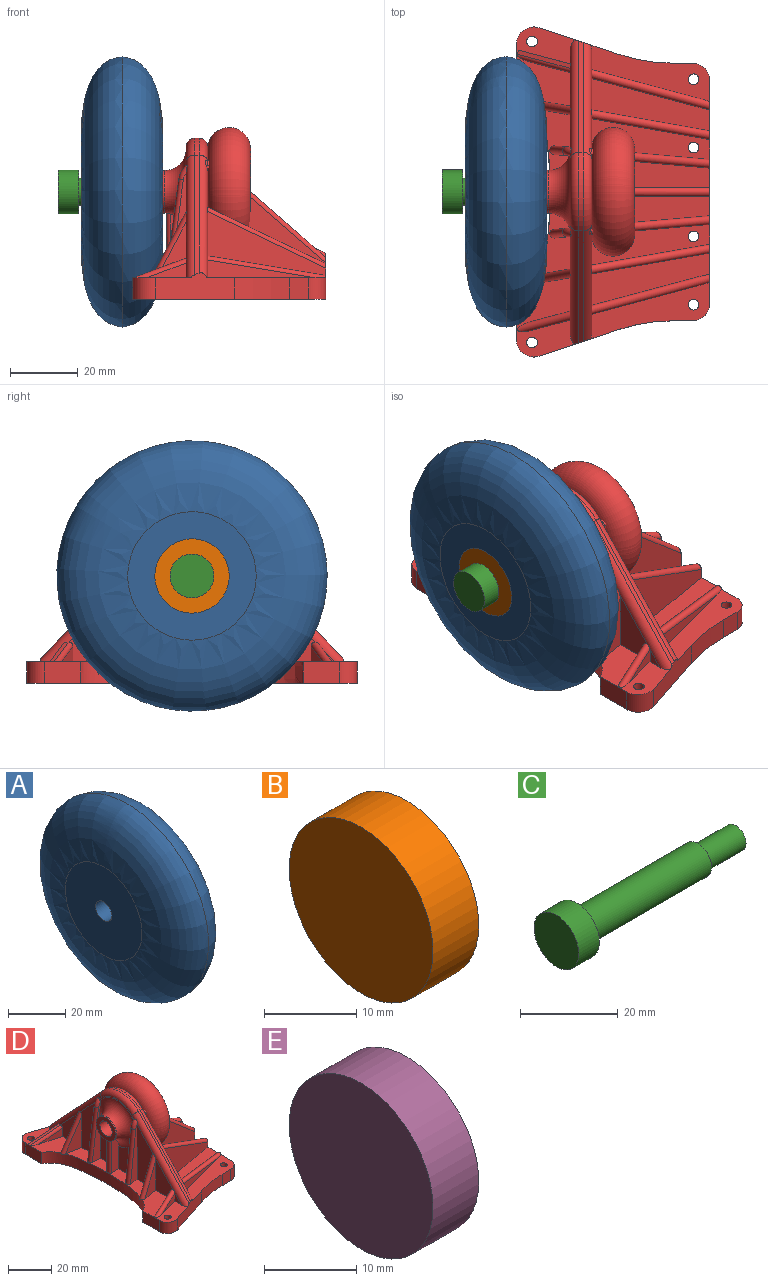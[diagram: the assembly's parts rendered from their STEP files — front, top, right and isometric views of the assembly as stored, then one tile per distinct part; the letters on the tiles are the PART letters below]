
ASSEMBLY  parts=5 mates=4
PART A: 5 faces, bbox 24x80x80 mm
  f0: cylinder r=4mm len=24mm, axis (-1,0,0), area 603.2mm2, adj f1,f4
  f1: plane 38x38mm, normal (1,0,0), area 1083.8mm2, adj f0,f2
  f2: revolved ~80x80mm, area 5252.7mm2, adj f1,f3
  f3: revolved ~80x80mm, area 5252.7mm2, adj f2,f4
  f4: plane 38x38mm, normal (-1,0,0), area 1083.8mm2, adj f0,f3
PART B: 3 faces, bbox 7x22x22 mm
  f0: plane 22x22mm, normal (1,0,0), area 380.1mm2, adj f1
  f1: cylinder r=11mm len=22mm, axis (-1,0,0), area 483.8mm2, adj f0,f2
  f2: plane 22x22mm, normal (-1,0,0), area 380.1mm2, adj f1
PART C: 7 faces, bbox 52x13x13 mm
  f0: cylinder r=6.5mm len=13mm, axis (1,0,0), area 245mm2, adj f1,f6
  f1: plane 13x13mm, normal (-1,0,0), area 132.7mm2, adj f0
  f2: plane 6x6mm, normal (1,0,0), area 28.3mm2, adj f3
  f3: cylinder r=3mm len=11mm, axis (1,0,0), area 207.3mm2, adj f2,f4
  f4: plane 8x8mm, normal (1,0,0), area 22mm2, adj f3,f5
  f5: cylinder r=4mm len=35mm, axis (1,0,0), area 879.6mm2, adj f4,f6
  f6: plane 13x13mm, normal (1,0,0), area 82.5mm2, adj f0,f5
PART D: 125 faces, bbox 58.6x98.1x52.8 mm
  f0: cylinder r=1.27mm len=29.7mm, axis (0.91,0,-0.42), area 124mm2, adj f1,f2,f50,f67,f68,f74
  f1: plane 35.02x19.43mm, normal (0,1,0), area 470mm2, adj f0,f27,f30,f32,f50,f74
  f2: plane 35.02x19.43mm, normal (0,-1,0), area 470mm2, adj f0,f30,f40,f45,f50,f74
  f3: plane 34.93x33.36mm, normal (-0.09,1,0), area 677.7mm2, adj f26,f30,f40,f45,f50,f109,f110
  f4: plane 35.43x33.46mm, normal (0.09,-1,0), area 688.9mm2, adj f39,f48,f50,f61,f63,f109,f110,f111
  f5: plane 34.97x19.63mm, normal (0.17,-0.98,0), area 399.1mm2, adj f34,f37,f50,f63,f123
  f6: plane 34.93x19.39mm, normal (-0.17,0.98,0), area 391.6mm2, adj f39,f48,f50,f123
  f7: plane 31.75x8.51mm, normal (0.26,-0.97,0), area 86.5mm2, adj f33,f34,f120
  f8: plane 31.09x8.33mm, normal (-0.26,0.97,0), area 83mm2, adj f34,f37,f120
  f9: plane 34.93x33.36mm, normal (-0.09,-1,0), area 677.7mm2, adj f26,f27,f30,f32,f50,f106,f107
  f10: plane 35.43x33.46mm, normal (0.09,1,0), area 688.9mm2, adj f16,f24,f25,f43,f50,f106,f107,f108
  f11: plane 34.97x19.63mm, normal (0.17,0.98,0), area 399.1mm2, adj f16,f20,f21,f50,f119
  f12: plane 34.93x19.39mm, normal (-0.17,-0.98,0), area 391.6mm2, adj f24,f25,f50,f119
  f13: plane 31.75x8.51mm, normal (0.26,0.97,0), area 86.5mm2, adj f20,f55,f116
  f14: plane 31.09x8.33mm, normal (-0.26,-0.97,0), area 83mm2, adj f20,f21,f116
  f15: plane 97.66x57.16mm, normal (0,0,-1), area 4244.1mm2, adj f46,f47,f50,f51,f52,f53,f54,f76
  f16: cylinder r=2.54mm len=36.96mm, axis (0,-0.68,0.73), area 184.4mm2, adj f10,f11,f20,f24,f26,f52,f55,f58
  f17: cylinder r=2.54mm len=37.76mm, axis (0,0.68,-0.73), area 189.7mm2, adj f18,f19,f22,f29,f41,f52,f58,f64
  f18: plane 18.03x11.41mm, normal (-1,0,0), area 125.3mm2, adj f17,f19,f88,f92,f117,f118
  f19: plane 23.53x17.25mm, normal (0,0,1), area 265mm2, adj f17,f18,f29,f52,f53,f76,f88,f91
  f20: plane 19.48x18.26mm, normal (1,0,0), area 152.7mm2, adj f11,f13,f14,f16,f21,f55,f116
  f21: plane 35.06x15.61mm, normal (0,0,1), area 269.9mm2, adj f11,f14,f20,f50,f116
  f22: plane 30.79x10.42mm, normal (-1,0,0), area 246.5mm2, adj f17,f23,f86,f89,f118
  f23: plane 49.04x9.21mm, normal (0,0,1), area 270.8mm2, adj f22,f28,f42,f49,f76,f77,f78,f79
  f24: plane 31.45x9.97mm, normal (1,0,0), area 239.9mm2, adj f10,f12,f16,f25,f43,f119
  f25: plane 34.93x12.06mm, normal (0,0,1), area 252.2mm2, adj f10,f12,f24,f50,f101
  f26: plane 20.52x5.66mm, normal (1,0,0), area 14.8mm2, adj f3,f9,f16,f30,f62,f63,f107,f110
  f27: plane 17.72x8.84mm, normal (1,0,0), area 127.6mm2, adj f1,f9,f30,f32
  f28: plane 18.51x9.4mm, normal (-1,0,0), area 137.7mm2, adj f23,f31,f78,f87
  f29: plane 4.42x4.13mm, normal (-1,0,0), area 9.1mm2, adj f17,f19,f91
  f30: torus R=12.7mm, axis (-1,0,0), area 409.3mm2, adj f1,f2,f3,f9,f26,f27,f40,f74
  f31: torus R=12.7mm, axis (1,0,0), area 480.9mm2, adj f28,f41,f42,f60,f77,f78,f80,f87
  f32: plane 34.93x8.84mm, normal (0,0,1), area 255.5mm2, adj f1,f9,f27,f50
  f33: plane 35.23x16.83mm, normal (0,0,1), area 262.3mm2, adj f7,f34,f47,f50,f54,f63,f99,f103
  f34: plane 19.48x18.26mm, normal (1,0,0), area 152.7mm2, adj f5,f7,f8,f33,f37,f63,f120
  f35: plane 4.42x4.13mm, normal (-1,0,0), area 9.1mm2, adj f36,f44,f85,f121
  f36: plane 23.53x17.25mm, normal (0,0,1), area 266.1mm2, adj f35,f38,f44,f46,f47,f76,f83,f84
  f37: plane 35.06x15.61mm, normal (0,0,1), area 269.9mm2, adj f5,f8,f34,f50,f120
  f38: plane 18.03x11.41mm, normal (-1,0,0), area 125.3mm2, adj f36,f44,f83,f84,f121,f122
  f39: plane 34.93x12.06mm, normal (0,0,1), area 252.2mm2, adj f4,f6,f48,f50,f97
  f40: plane 17.72x8.84mm, normal (1,0,0), area 127.6mm2, adj f2,f3,f30,f45
  f41: plane 22.51x6.67mm, normal (-1,0,0), area 16.7mm2, adj f17,f31,f44,f64,f113,f114
  f42: plane 18.51x9.4mm, normal (-1,0,0), area 137.7mm2, adj f23,f31,f77,f80
  f43: torus R=12.7mm, axis (-1,0,0), area 3183.7mm2, adj f10,f24
  f44: cylinder r=2.54mm len=37.76mm, axis (0,0.68,0.73), area 190.1mm2, adj f35,f36,f38,f41,f47,f49,f56,f64
  f45: plane 34.93x8.84mm, normal (0,0,1), area 255.5mm2, adj f2,f3,f40,f50
  f46: plane 10.9x6.35mm, normal (-1,0,0), area 69.2mm2, adj f15,f36,f76,f95
  f47: plane 23.59x7.86mm, normal (0.32,-0.95,0), area 162.9mm2, adj f15,f33,f36,f44,f56,f63,f95,f105
  f48: plane 31.45x9.97mm, normal (1,0,0), area 239.9mm2, adj f4,f6,f39,f61,f63,f123
  f49: plane 30.79x10.42mm, normal (-1,0,0), area 246.5mm2, adj f23,f44,f79,f82,f122
  f50: plane 66.3x13.92mm, normal (1,0,0), area 488.6mm2, adj f0,f1,f2,f3,f4,f5,f6,f9
  f51: plane 6.35x5.73mm, normal (0,1,0), area 36.4mm2, adj f15,f55,f102,f104
  f52: plane 23.59x7.86mm, normal (0.32,0.95,0), area 162.9mm2, adj f15,f16,f17,f19,f55,f58,f94,f104
  f53: plane 10.9x6.35mm, normal (-1,0,0), area 69.2mm2, adj f15,f19,f76,f94
  f54: plane 6.35x5.73mm, normal (0,-1,0), area 36.4mm2, adj f15,f33,f103,f105
  f55: plane 35.23x16.83mm, normal (0,0,1), area 262.3mm2, adj f13,f16,f20,f50,f51,f52,f96,f102
  f56: plane 35.34x33.07mm, normal (0,-0.73,0.68), area 61.1mm2, adj f44,f47,f57,f63
  f57: cylinder r=15.88mm len=23.18mm, axis (1,0,0), area 33mm2, adj f56,f58,f62,f64
  f58: plane 35.34x33.07mm, normal (0,0.73,0.68), area 61.1mm2, adj f16,f17,f52,f57
  f59: plane 12.7x12.7mm, normal (-1,0,0), area 76.4mm2, adj f60,f65
  f60: cylinder r=6.35mm len=12.7mm, axis (-1,0,0), area 25.3mm2, adj f31,f59
  f61: torus R=12.7mm, axis (-1,0,0), area 3183.7mm2, adj f4,f48
  f62: torus R=13.33mm, axis (-1,0,0), area 97.7mm2, adj f16,f26,f57,f63
  f63: cylinder r=2.54mm len=36.96mm, axis (0,-0.68,-0.73), area 184.4mm2, adj f4,f5,f26,f33,f34,f47,f48,f56
  f64: torus R=13.33mm, axis (1,0,0), area 97.7mm2, adj f17,f41,f44,f57
  f65: cylinder r=4mm len=10.16mm, axis (1,0,0), area 255.3mm2, adj f59,f66
  f66: plane 8x8mm, normal (-1,0,0), area 22mm2, adj f65,f75
  f67: plane 7.4x5.22mm, normal (0,0.5,0.87), area 33.6mm2, adj f0,f68,f72,f73,f74
  f68: plane 7.4x5.22mm, normal (0,-0.5,0.87), area 33.6mm2, adj f0,f67,f69,f73,f74
  f69: plane 5.8x5.77mm, normal (0,-1,0), area 32.6mm2, adj f68,f70,f73,f74
  f70: plane 5.8x5mm, normal (0,-0.5,-0.87), area 32.6mm2, adj f69,f71,f73,f74
  f71: plane 5.8x5mm, normal (0,0.5,-0.87), area 32.6mm2, adj f70,f72,f73,f74
  f72: plane 5.8x5.77mm, normal (0,1,0), area 32.6mm2, adj f67,f71,f73,f74
  f73: plane 11.55x10mm, normal (1,0,0), area 58.3mm2, adj f67,f68,f69,f70,f71,f72,f75
  f74: torus R=4.02mm, axis (-1,0,0), area 76.4mm2, adj f0,f1,f2,f30,f67,f68,f69,f70
  f75: cylinder r=3mm len=6mm, axis (-1,0,0), area 78.4mm2, adj f66,f73
  f76: extruded ~65.71x9.96mm, area 456.5mm2, adj f15,f19,f23,f36,f46,f53,f81,f90
  f77: plane 19.02x4.67mm, normal (0,-1,0), area 78.9mm2, adj f23,f31,f42,f124
  f78: plane 19.02x4.67mm, normal (0,1,0), area 78.9mm2, adj f23,f28,f31,f124
  f79: plane 31.23x4.64mm, normal (0.09,-1,0), area 80.9mm2, adj f23,f44,f49,f114,f115
  f80: plane 31.49x4.85mm, normal (-0.09,1,0), area 85.5mm2, adj f23,f31,f42,f114,f115
  f81: plane 2.27x1.45mm, normal (0,0,-1), area 1.6mm2, adj f76,f82,f122
  f82: plane 17.38x9.11mm, normal (-0.17,0.98,0), area 80.4mm2, adj f23,f49,f81,f122
  f83: plane 16.54x8.67mm, normal (0.17,-0.98,0), area 72.8mm2, adj f36,f38,f122
  f84: plane 12.33x4.61mm, normal (-0.26,0.97,0), area 29.4mm2, adj f36,f38,f121
  f85: plane 11.67x4.36mm, normal (0.26,-0.97,0), area 26.4mm2, adj f35,f36,f121
  f86: plane 31.23x4.64mm, normal (0.09,1,0), area 80.9mm2, adj f17,f22,f23,f112,f113
  f87: plane 31.49x4.85mm, normal (-0.09,-1,0), area 85.5mm2, adj f23,f28,f31,f112,f113
  f88: plane 16.54x8.67mm, normal (0.17,0.98,0), area 72.8mm2, adj f18,f19,f118
  f89: plane 17.38x9.11mm, normal (-0.17,-0.98,0), area 80.4mm2, adj f22,f23,f90,f118
  f90: plane 2.27x1.45mm, normal (0,0,-1), area 1.6mm2, adj f76,f89,f118
  f91: plane 15.45x5.77mm, normal (0.26,0.97,0), area 45.3mm2, adj f17,f19,f29,f93
  f92: plane 12.33x4.61mm, normal (-0.26,-0.97,0), area 29.4mm2, adj f18,f19,f117
  f93: plane 15.78x5.83mm, normal (-0.33,0.09,0.94), area 21.7mm2, adj f17,f19,f91,f117
  f94: cylinder r=5.08mm len=6.69mm, axis (0,0,-1), area 61mm2, adj f15,f19,f52,f53
  f95: cylinder r=5.08mm len=6.69mm, axis (0,0,-1), area 61mm2, adj f15,f36,f46,f47
  f96: cylinder r=1.59mm len=6.35mm, axis (0,0,-1), area 63.3mm2, adj f15,f55
  f97: cylinder r=1.59mm len=6.35mm, axis (0,0,-1), area 63.3mm2, adj f15,f39
  f98: cylinder r=1.59mm len=6.35mm, axis (0,0,-1), area 63.3mm2, adj f15,f36
  f99: cylinder r=1.59mm len=6.35mm, axis (0,0,-1), area 63.3mm2, adj f15,f33
  f100: cylinder r=1.59mm len=6.35mm, axis (0,0,-1), area 63.3mm2, adj f15,f19
  f101: cylinder r=1.59mm len=6.35mm, axis (0,0,-1), area 63.3mm2, adj f15,f25
  f102: cylinder r=5.08mm len=6.35mm, axis (0,0,1), area 50.7mm2, adj f15,f50,f51,f55
  f103: cylinder r=5.08mm len=6.35mm, axis (0,0,-1), area 50.7mm2, adj f15,f33,f50,f54
  f104: cylinder r=50.8mm len=16.06mm, axis (0,0,-1), area 103.8mm2, adj f15,f51,f52,f55
  f105: cylinder r=50.8mm len=16.06mm, axis (0,0,1), area 103.8mm2, adj f15,f33,f47,f54
  f106: cylinder r=1.27mm len=32.88mm, axis (0.75,-0.07,-0.66), area 166.1mm2, adj f9,f10,f50,f107
  f107: torus R=5.08mm, axis (0.09,1,0), area 16.4mm2, adj f9,f10,f16,f26,f106,f108
  f108: cylinder r=1.27mm len=1.59mm, axis (1,-0.09,0), area 0.9mm2, adj f10,f16,f107
  f109: cylinder r=1.27mm len=32.88mm, axis (-0.75,-0.07,0.66), area 166.1mm2, adj f3,f4,f50,f110
  f110: torus R=5.08mm, axis (0.09,-1,0), area 16.4mm2, adj f3,f4,f26,f63,f109,f111
  f111: cylinder r=1.27mm len=1.59mm, axis (-1,-0.09,0), area 0.9mm2, adj f4,f63,f110
  f112: cylinder r=1.27mm len=29.14mm, axis (-0.13,0.01,-0.99), area 116.6mm2, adj f23,f86,f87,f113
  f113: torus R=5.08mm, axis (0.09,1,0), area 16.4mm2, adj f17,f31,f41,f86,f87,f112
  f114: torus R=5.08mm, axis (0.09,-1,0), area 16.4mm2, adj f31,f41,f44,f79,f80,f115
  f115: cylinder r=1.27mm len=29.14mm, axis (0.13,0.01,0.99), area 116.6mm2, adj f23,f79,f80,f114
  f116: cylinder r=1.27mm len=36.16mm, axis (-0.95,0.26,0.16), area 143.6mm2, adj f13,f14,f20,f21,f50,f55
  f117: cylinder r=1.27mm len=15.93mm, axis (0.91,-0.24,0.34), area 31.9mm2, adj f17,f18,f19,f92,f93
  f118: cylinder r=1.27mm len=20.31mm, axis (-0.46,0.08,-0.88), area 84.3mm2, adj f17,f18,f19,f22,f88,f89,f90
  f119: cylinder r=1.27mm len=36.64mm, axis (-0.89,0.16,0.43), area 156.6mm2, adj f11,f12,f16,f24,f50
  f120: cylinder r=1.27mm len=36.16mm, axis (0.95,0.26,-0.16), area 143.6mm2, adj f7,f8,f33,f34,f37,f50
  f121: cylinder r=1.27mm len=16.6mm, axis (0.91,0.24,0.34), area 62.8mm2, adj f35,f36,f38,f44,f84,f85
  f122: cylinder r=1.27mm len=20.31mm, axis (0.46,0.08,0.88), area 84.3mm2, adj f36,f38,f44,f49,f81,f82,f83
  f123: cylinder r=1.27mm len=36.64mm, axis (0.89,0.16,-0.43), area 156.6mm2, adj f5,f6,f48,f50,f63
  f124: cylinder r=1.27mm len=19.03mm, axis (0,0,1), area 75.7mm2, adj f23,f31,f77,f78
PART E: 3 faces, bbox 7x22x22 mm
  f0: plane 22x22mm, normal (-1,0,0), area 380.1mm2, adj f2
  f1: plane 22x22mm, normal (1,0,0), area 380.1mm2, adj f2
  f2: cylinder r=11mm len=22mm, axis (-1,0,0), area 483.8mm2, adj f0,f1
PLACE A rot(axis=(-1,0,0),58.9deg) t=(-36.39,-16.3,32.66)mm
PLACE B rot(axis=(1,0,0),31.1deg) t=(-36.39,27.29,21.9)mm
PLACE C t=(-36.39,10.87,17.33)mm
PLACE D t=(-36.39,10.87,17.33)mm fixed
PLACE E t=(-36.39,10.87,17.33)mm
MATE revolute A.f0 <-> E.f2  axis (1,0,0) through (-46.55,10.87,49.08)mm
MATE revolute B.f1 <-> A.f0  axis (-1,0,0) through (-70.55,10.87,49.08)mm
MATE revolute E.f2 <-> D.f60  axis (1,0,0) through (-46.55,10.87,49.08)mm
MATE revolute D.f75 <-> C.f0  axis (-1,0,0) through (-36.39,10.87,49.08)mm
